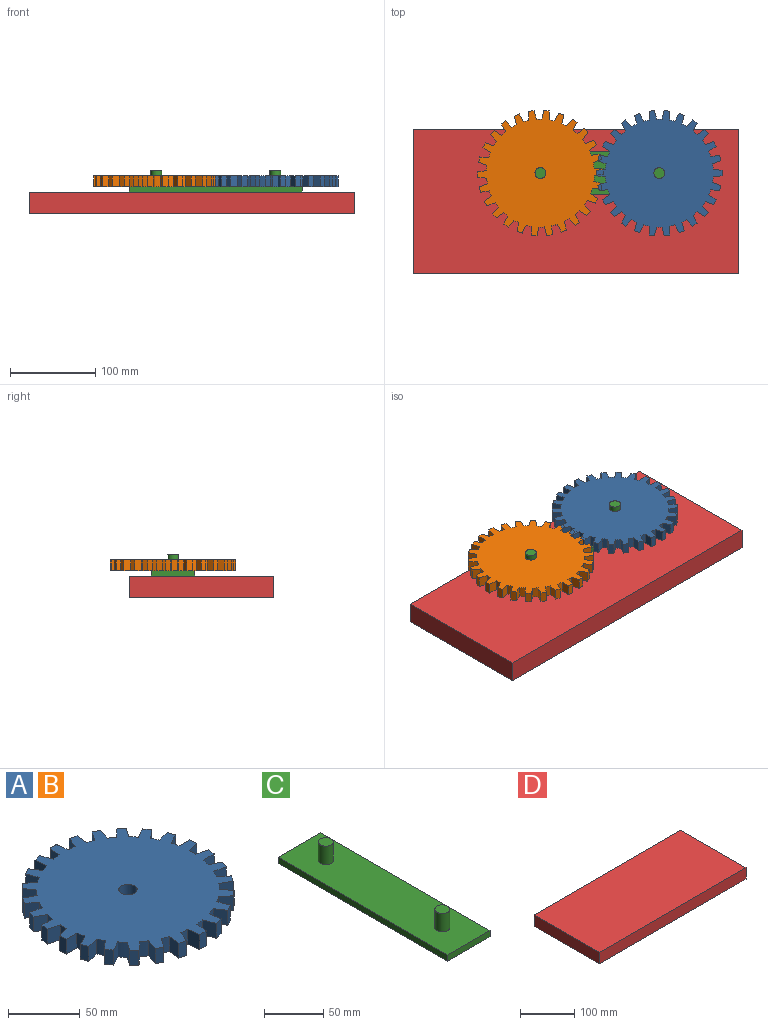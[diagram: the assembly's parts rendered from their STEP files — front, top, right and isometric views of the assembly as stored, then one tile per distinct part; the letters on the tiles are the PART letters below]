
ASSEMBLY  parts=4 mates=4
PART A: 109 faces, bbox 147x147.3x12.7 mm
  f0: plane 12.7x6.35mm, normal (0,-1,0), area 80.6mm2, adj f1,f106,f107,f108
  f1: plane 12.7x10.32mm, normal (0.99,-0.12,0), area 132mm2, adj f0,f2,f107,f108
  f2: cylinder r=63.5mm len=12.7mm, axis (0,0,-1), area 82mm2, adj f1,f3,f107,f108
  f3: plane 12.7x9.71mm, normal (-0.93,-0.36,0), area 132mm2, adj f2,f4,f107,f108
  f4: plane 12.7x6.17mm, normal (0.24,-0.97,0), area 80.6mm2, adj f3,f5,f107,f108
  f5: plane 12.7x10.32mm, normal (0.99,0.12,0), area 132mm2, adj f4,f6,f107,f108
  f6: cylinder r=63.5mm len=12.7mm, axis (0,0,-1), area 82mm2, adj f5,f7,f107,f108
  f7: plane 12.7x8.55mm, normal (-0.82,-0.57,0), area 132mm2, adj f6,f8,f107,f108
  f8: plane 12.7x5.62mm, normal (0.46,-0.89,0), area 80.6mm2, adj f7,f9,f107,f108
  f9: plane 12.7x9.72mm, normal (0.94,0.35,0), area 132mm2, adj f8,f10,f107,f108
  f10: cylinder r=63.5mm len=12.7mm, axis (0,0,-1), area 82mm2, adj f9,f11,f107,f108
  f11: plane 12.7x7.79mm, normal (-0.66,-0.75,0), area 132mm2, adj f10,f12,f107,f108
  f12: plane 12.7x4.75mm, normal (0.66,-0.75,0), area 80.6mm2, adj f11,f13,f107,f108
  f13: plane 12.7x8.56mm, normal (0.82,0.57,0), area 132mm2, adj f12,f14,f107,f108
  f14: cylinder r=63.5mm len=12.7mm, axis (0,0,-1), area 82mm2, adj f13,f15,f107,f108
  f15: plane 12.7x9.21mm, normal (-0.46,-0.89,0), area 132mm2, adj f14,f16,f107,f108
  f16: plane 12.7x5.23mm, normal (0.82,-0.57,0), area 80.6mm2, adj f15,f17,f107,f108
  f17: plane 12.7x7.77mm, normal (0.66,0.75,0), area 132mm2, adj f16,f18,f107,f108
  f18: cylinder r=63.5mm len=12.7mm, axis (0,0,-1), area 82mm2, adj f17,f19,f107,f108
  f19: plane 12.7x10.09mm, normal (-0.24,-0.97,0), area 132mm2, adj f18,f20,f107,f108
  f20: plane 12.7x5.94mm, normal (0.94,-0.35,0), area 80.6mm2, adj f19,f21,f107,f108
  f21: plane 12.7x9.2mm, normal (0.47,0.88,0), area 132mm2, adj f20,f22,f107,f108
  f22: cylinder r=63.5mm len=12.7mm, axis (0,0,-1), area 82mm2, adj f21,f23,f107,f108
  f23: plane 12.7x10.39mm, normal (0,-1,0), area 132mm2, adj f22,f24,f107,f108
  f24: plane 12.7x6.3mm, normal (0.99,-0.12,0), area 80.6mm2, adj f23,f25,f107,f108
  f25: plane 12.7x10.09mm, normal (0.24,0.97,0), area 132mm2, adj f24,f26,f107,f108
  f26: cylinder r=63.5mm len=12.7mm, axis (0,0,-1), area 82mm2, adj f25,f27,f107,f108
  f27: plane 12.7x10.09mm, normal (0.24,-0.97,0), area 132mm2, adj f26,f28,f107,f108
  f28: plane 12.7x6.3mm, normal (0.99,0.12,0), area 80.6mm2, adj f27,f29,f107,f108
  f29: plane 12.7x10.39mm, normal (0,1,0), area 132mm2, adj f28,f30,f107,f108
  f30: cylinder r=63.5mm len=12.7mm, axis (0,0,-1), area 82mm2, adj f29,f31,f107,f108
  f31: plane 12.7x9.2mm, normal (0.47,-0.88,0), area 132mm2, adj f30,f32,f107,f108
  f32: plane 12.7x5.94mm, normal (0.94,0.35,0), area 80.6mm2, adj f31,f33,f107,f108
  f33: plane 12.7x10.09mm, normal (-0.24,0.97,0), area 132mm2, adj f32,f34,f107,f108
  f34: cylinder r=63.5mm len=12.7mm, axis (0,0,-1), area 82mm2, adj f33,f35,f107,f108
  f35: plane 12.7x7.77mm, normal (0.66,-0.75,0), area 132mm2, adj f34,f36,f107,f108
  f36: plane 12.7x5.23mm, normal (0.82,0.57,0), area 80.6mm2, adj f35,f37,f107,f108
  f37: plane 12.7x9.21mm, normal (-0.46,0.89,0), area 132mm2, adj f36,f38,f107,f108
  f38: cylinder r=63.5mm len=12.7mm, axis (0,0,-1), area 82mm2, adj f37,f39,f107,f108
  f39: plane 12.7x8.56mm, normal (0.82,-0.57,0), area 132mm2, adj f38,f40,f107,f108
  f40: plane 12.7x4.75mm, normal (0.66,0.75,0), area 80.6mm2, adj f39,f41,f107,f108
  f41: plane 12.7x7.79mm, normal (-0.66,0.75,0), area 132mm2, adj f40,f42,f107,f108
  f42: cylinder r=63.5mm len=12.7mm, axis (0,0,-1), area 82mm2, adj f41,f43,f107,f108
  f43: plane 12.7x9.72mm, normal (0.94,-0.35,0), area 132mm2, adj f42,f44,f107,f108
  f44: plane 12.7x5.62mm, normal (0.46,0.89,0), area 80.6mm2, adj f43,f45,f107,f108
  f45: plane 12.7x8.55mm, normal (-0.82,0.57,0), area 132mm2, adj f44,f46,f107,f108
  f46: cylinder r=63.5mm len=12.7mm, axis (0,0,-1), area 82mm2, adj f45,f47,f107,f108
  f47: plane 12.7x10.32mm, normal (0.99,-0.12,0), area 132mm2, adj f46,f48,f107,f108
  f48: plane 12.7x6.17mm, normal (0.24,0.97,0), area 80.6mm2, adj f47,f49,f107,f108
  f49: plane 12.7x9.71mm, normal (-0.93,0.36,0), area 132mm2, adj f48,f50,f107,f108
  f50: cylinder r=63.5mm len=12.7mm, axis (0,0,-1), area 82mm2, adj f49,f51,f107,f108
  f51: plane 12.7x9.2mm, normal (0.99,0.12,0), area 117.7mm2, adj f50,f52,f107,f108
  f52: cylinder r=1.27mm len=12.7mm, axis (0,0,-1), area 23.4mm2, adj f51,f53,f107,f108
  f53: plane 12.7x4.1mm, normal (0,1,0), area 52.1mm2, adj f52,f54,f107,f108
  f54: cylinder r=1.27mm len=12.7mm, axis (0,0,-1), area 23.4mm2, adj f53,f55,f107,f108
  f55: plane 12.7x9.2mm, normal (-0.99,0.12,0), area 117.7mm2, adj f54,f56,f107,f108
  f56: cylinder r=63.5mm len=12.7mm, axis (0,0,-1), area 82mm2, adj f55,f57,f107,f108
  f57: plane 12.7x9.71mm, normal (0.93,0.36,0), area 132mm2, adj f56,f58,f107,f108
  f58: plane 12.7x6.17mm, normal (-0.24,0.97,0), area 80.6mm2, adj f57,f59,f107,f108
  f59: plane 12.7x10.32mm, normal (-0.99,-0.12,0), area 132mm2, adj f58,f60,f107,f108
  f60: cylinder r=63.5mm len=12.7mm, axis (0,0,-1), area 82mm2, adj f59,f61,f107,f108
  f61: plane 12.7x8.55mm, normal (0.82,0.57,0), area 132mm2, adj f60,f62,f107,f108
  f62: plane 12.7x5.62mm, normal (-0.46,0.89,0), area 80.6mm2, adj f61,f63,f107,f108
  f63: plane 12.7x9.72mm, normal (-0.94,-0.35,0), area 132mm2, adj f62,f64,f107,f108
  f64: cylinder r=63.5mm len=12.7mm, axis (0,0,-1), area 82mm2, adj f63,f65,f107,f108
  f65: plane 12.7x7.79mm, normal (0.66,0.75,0), area 132mm2, adj f64,f66,f107,f108
  f66: plane 12.7x4.75mm, normal (-0.66,0.75,0), area 80.6mm2, adj f65,f67,f107,f108
  f67: plane 12.7x8.56mm, normal (-0.82,-0.57,0), area 132mm2, adj f66,f68,f107,f108
  f68: cylinder r=63.5mm len=12.7mm, axis (0,0,-1), area 82mm2, adj f67,f69,f107,f108
  f69: plane 12.7x9.21mm, normal (0.46,0.89,0), area 132mm2, adj f68,f70,f107,f108
  f70: plane 12.7x5.23mm, normal (-0.82,0.57,0), area 80.6mm2, adj f69,f71,f107,f108
  f71: plane 12.7x7.77mm, normal (-0.66,-0.75,0), area 132mm2, adj f70,f72,f107,f108
  f72: cylinder r=63.5mm len=12.7mm, axis (0,0,-1), area 82mm2, adj f71,f73,f107,f108
  f73: plane 12.7x10.09mm, normal (0.24,0.97,0), area 132mm2, adj f72,f74,f107,f108
  f74: plane 12.7x5.94mm, normal (-0.94,0.35,0), area 80.6mm2, adj f73,f75,f107,f108
  f75: plane 12.7x9.2mm, normal (-0.47,-0.88,0), area 132mm2, adj f74,f76,f107,f108
  f76: cylinder r=63.5mm len=12.7mm, axis (0,0,-1), area 82mm2, adj f75,f77,f107,f108
  f77: plane 12.7x10.39mm, normal (0,1,0), area 132mm2, adj f76,f78,f107,f108
  f78: plane 12.7x6.3mm, normal (-0.99,0.12,0), area 80.6mm2, adj f77,f79,f107,f108
  f79: plane 12.7x10.09mm, normal (-0.24,-0.97,0), area 132mm2, adj f78,f80,f107,f108
  f80: cylinder r=63.5mm len=12.7mm, axis (0,0,-1), area 82mm2, adj f79,f81,f107,f108
  f81: plane 12.7x10.09mm, normal (-0.24,0.97,0), area 132mm2, adj f80,f82,f107,f108
  f82: plane 12.7x6.3mm, normal (-0.99,-0.12,0), area 80.6mm2, adj f81,f83,f107,f108
  f83: plane 12.7x10.39mm, normal (0,-1,0), area 132mm2, adj f82,f84,f107,f108
  f84: cylinder r=63.5mm len=12.7mm, axis (0,0,-1), area 82mm2, adj f83,f85,f107,f108
  f85: plane 12.7x9.2mm, normal (-0.47,0.88,0), area 132mm2, adj f84,f86,f107,f108
  f86: plane 12.7x5.94mm, normal (-0.94,-0.35,0), area 80.6mm2, adj f85,f87,f107,f108
  f87: plane 12.7x10.09mm, normal (0.24,-0.97,0), area 132mm2, adj f86,f88,f107,f108
  f88: cylinder r=63.5mm len=12.7mm, axis (0,0,-1), area 82mm2, adj f87,f89,f107,f108
  f89: plane 12.7x7.77mm, normal (-0.66,0.75,0), area 132mm2, adj f88,f90,f107,f108
  f90: plane 12.7x5.23mm, normal (-0.82,-0.57,0), area 80.6mm2, adj f89,f91,f107,f108
  f91: plane 12.7x9.21mm, normal (0.46,-0.89,0), area 132mm2, adj f90,f92,f107,f108
  f92: cylinder r=63.5mm len=12.7mm, axis (0,0,-1), area 82mm2, adj f91,f93,f107,f108
  f93: plane 12.7x8.56mm, normal (-0.82,0.57,0), area 132mm2, adj f92,f94,f107,f108
  f94: plane 12.7x4.75mm, normal (-0.66,-0.75,0), area 80.6mm2, adj f93,f95,f107,f108
  f95: plane 12.7x7.79mm, normal (0.66,-0.75,0), area 132mm2, adj f94,f96,f107,f108
  f96: cylinder r=63.5mm len=12.7mm, axis (0,0,-1), area 82mm2, adj f95,f97,f107,f108
  f97: plane 12.7x9.72mm, normal (-0.94,0.35,0), area 132mm2, adj f96,f98,f107,f108
  f98: plane 12.7x5.62mm, normal (-0.46,-0.89,0), area 80.6mm2, adj f97,f99,f107,f108
  f99: plane 12.7x8.55mm, normal (0.82,-0.57,0), area 132mm2, adj f98,f100,f107,f108
  f100: cylinder r=63.5mm len=12.7mm, axis (0,0,-1), area 82mm2, adj f99,f101,f107,f108
  f101: plane 12.7x10.32mm, normal (-0.99,0.12,0), area 132mm2, adj f100,f102,f107,f108
  f102: plane 12.7x6.17mm, normal (-0.24,-0.97,0), area 80.6mm2, adj f101,f103,f107,f108
  f103: plane 12.7x9.71mm, normal (0.93,-0.36,0), area 132mm2, adj f102,f104,f107,f108
  f104: cylinder r=63.5mm len=12.7mm, axis (0,0,-1), area 82mm2, adj f103,f106,f107,f108
  f105: cylinder r=6.35mm len=12.7mm, axis (0,0,-1), area 506.7mm2, adj f107,f108
  f106: plane 12.7x10.32mm, normal (-0.99,-0.12,0), area 132mm2, adj f0,f104,f107,f108
  f107: plane 147.32x147.01mm, normal (0,0,1), area 14559.5mm2, adj f0,f1,f2,f3,f4,f5,f6,f7
  f108: plane 147.32x147.01mm, normal (0,0,-1), area 14559.5mm2, adj f0,f1,f2,f3,f4,f5,f6,f7
PART B: same geometry as A
PART C: 10 faces, bbox 50.8x203.2x25.4 mm
  f0: plane 203.2x6.35mm, normal (-1,0,0), area 1290.3mm2, adj f1,f3,f4,f5
  f1: plane 50.8x6.35mm, normal (0,-1,0), area 322.6mm2, adj f0,f2,f4,f5
  f2: plane 203.2x6.35mm, normal (1,0,0), area 1290.3mm2, adj f1,f3,f4,f5
  f3: plane 50.8x6.35mm, normal (0,1,0), area 322.6mm2, adj f0,f2,f4,f5
  f4: plane 203.2x50.8mm, normal (0,0,1), area 10069.2mm2, adj f0,f1,f2,f3,f6,f8
  f5: plane 203.2x50.8mm, normal (0,0,-1), area 10322.6mm2, adj f0,f1,f2,f3
  f6: cylinder r=6.35mm len=19.05mm, axis (0,0,-1), area 760.1mm2, adj f4,f7
  f7: plane 12.7x12.7mm, normal (0,0,1), area 126.7mm2, adj f6
  f8: cylinder r=6.35mm len=19.05mm, axis (0,0,-1), area 760.1mm2, adj f4,f9
  f9: plane 12.7x12.7mm, normal (0,0,1), area 126.7mm2, adj f8
PART D: 6 faces, bbox 382.1x169.5x25.4 mm
  f0: plane 382.09x25.4mm, normal (0,-1,0), area 9705mm2, adj f1,f3,f4,f5
  f1: plane 169.48x25.4mm, normal (1,0,0), area 4304.8mm2, adj f0,f2,f4,f5
  f2: plane 382.09x25.4mm, normal (0,1,0), area 9705mm2, adj f1,f3,f4,f5
  f3: plane 169.48x25.4mm, normal (-1,0,0), area 4304.8mm2, adj f0,f2,f4,f5
  f4: plane 382.09x169.48mm, normal (0,0,1), area 64755.6mm2, adj f0,f1,f2,f3
  f5: plane 382.09x169.48mm, normal (0,0,-1), area 64755.6mm2, adj f0,f1,f2,f3
PLACE A rot(axis=(0,0,1),90deg) t=(86.2,238.38,31.75)mm
PLACE B rot(axis=(0,0,-1),47.1deg) t=(-53.5,238.38,31.75)mm
PLACE C rot(axis=(0,0,-1),90deg) t=(82.33,412.41,25.4)mm
PLACE D at identity fixed
MATE revolute B.f105 <-> C.f6  axis (0,0,-1) through (-53.5,238.38,31.75)mm
MATE slider C.f8 <-> A.f105  axis (0,0,-1) through (86.2,238.38,31.75)mm
MATE planar C.f5 <-> D.f4  axis (0,0,-1) through (16.35,238.38,25.4)mm
MATE parallel C.f2 <-> D.f0  axis (0,-1,0) through (16.35,212.98,28.58)mm
